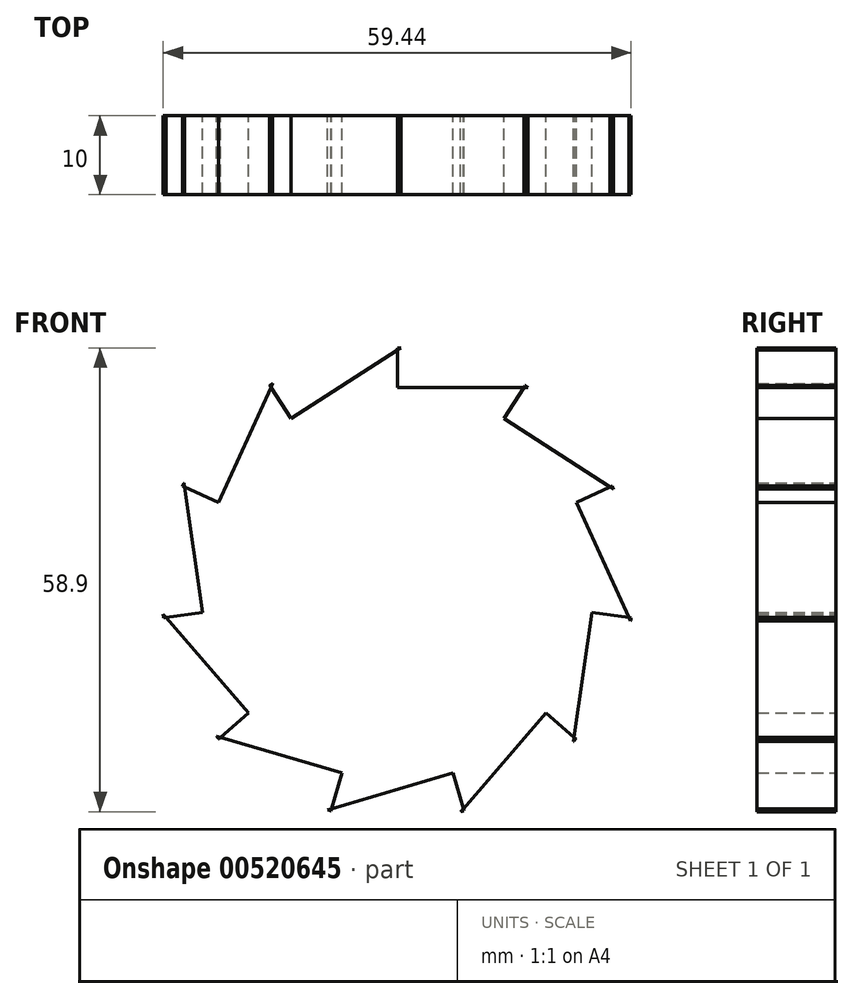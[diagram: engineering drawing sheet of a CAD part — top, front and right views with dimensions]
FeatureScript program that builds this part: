
annotation { "Feature Type Name" : "Feature", "Feature Type Description" : "" }
export const myFeature = defineFeature(function(context is Context, id is Id, definition is map)
    precondition{}
    {
        {
            var Q0;
            Q0=qCreatedBy(makeId("Front.planeOp"),FACE);
            var sketch = newSketch(context, id + "F0", { "sketchPlane" : qUnion([Q0])});
            skArc(sketch, "E0", {"start": v(16.58, 25) * mm, "mid": v(16.4, 25.12) * mm, "end": v(16.22, 25.24) * mm});
            skLineSegment(sketch, "E1", {"start": v(0, 25) * mm, "end": v(16.58, 25) * mm});
            skLineSegment(sketch, "E2", {"start": v(0, 30) * mm, "end": v(0, 25) * mm});
            skLineSegment(sketch, "E3.1.0", {"start": v(-13.52, 21.03) * mm, "end": v(0.43, 30) * mm});
            skLineSegment(sketch, "E3.1.1", {"start": v(-16.22, 25.24) * mm, "end": v(-13.52, 21.03) * mm});
            skLineSegment(sketch, "E3.2.0", {"start": v(-22.74, 10.39) * mm, "end": v(-15.85, 25.47) * mm});
            skLineSegment(sketch, "E3.2.1", {"start": v(-27.29, 12.46) * mm, "end": v(-22.74, 10.39) * mm});
            skLineSegment(sketch, "E3.3.0", {"start": v(-24.75, -3.56) * mm, "end": v(-27.1, 12.86) * mm});
            skLineSegment(sketch, "E3.3.1", {"start": v(-29.7, -4.27) * mm, "end": v(-24.75, -3.56) * mm});
            skLineSegment(sketch, "E3.4.0", {"start": v(-18.9, -16.37) * mm, "end": v(-29.75, -3.84) * mm});
            skLineSegment(sketch, "E3.4.1", {"start": v(-22.67, -19.65) * mm, "end": v(-18.9, -16.37) * mm});
            skLineSegment(sketch, "E3.5.0", {"start": v(-7.04, -23.99) * mm, "end": v(-22.95, -19.32) * mm});
            skLineSegment(sketch, "E3.5.1", {"start": v(-8.45, -28.78) * mm, "end": v(-7.04, -23.99) * mm});
            skLineSegment(sketch, "E3.6.0", {"start": v(7.04, -23.99) * mm, "end": v(-8.87, -28.66) * mm});
            skLineSegment(sketch, "E3.6.1", {"start": v(8.45, -28.78) * mm, "end": v(7.04, -23.99) * mm});
            skLineSegment(sketch, "E3.7.0", {"start": v(18.9, -16.37) * mm, "end": v(8.03, -28.9) * mm});
            skLineSegment(sketch, "E3.7.1", {"start": v(22.67, -19.65) * mm, "end": v(18.9, -16.37) * mm});
            skLineSegment(sketch, "E3.8.0", {"start": v(24.75, -3.56) * mm, "end": v(22.39, -19.97) * mm});
            skLineSegment(sketch, "E3.8.1", {"start": v(29.7, -4.27) * mm, "end": v(24.75, -3.56) * mm});
            skLineSegment(sketch, "E3.9.0", {"start": v(22.74, 10.39) * mm, "end": v(29.63, -4.7) * mm});
            skLineSegment(sketch, "E3.9.1", {"start": v(27.29, 12.46) * mm, "end": v(22.74, 10.39) * mm});
            skLineSegment(sketch, "E3.10.0", {"start": v(13.52, 21.03) * mm, "end": v(27.47, 12.07) * mm});
            skLineSegment(sketch, "E3.10.1", {"start": v(16.22, 25.24) * mm, "end": v(13.52, 21.03) * mm});
            skArc(sketch, "E4.trimOffspring", {"start": v(27.47, 12.07) * mm, "mid": v(27.38, 12.26) * mm, "end": v(27.29, 12.46) * mm});
            skArc(sketch, "E5.trimOffspring", {"start": v(29.63, -4.7) * mm, "mid": v(29.66, -4.48) * mm, "end": v(29.7, -4.27) * mm});
            skArc(sketch, "E6.trimOffspring", {"start": v(0.43, 30) * mm, "mid": v(0.22, 30) * mm, "end": v(0, 30) * mm});
            skArc(sketch, "E7.trimOffspring", {"start": v(-15.85, 25.47) * mm, "mid": v(-16.04, 25.35) * mm, "end": v(-16.22, 25.24) * mm});
            skArc(sketch, "E8.trimOffspring", {"start": v(-27.1, 12.86) * mm, "mid": v(-27.2, 12.66) * mm, "end": v(-27.29, 12.46) * mm});
            skArc(sketch, "E9.trimOffspring", {"start": v(-29.75, -3.84) * mm, "mid": v(-29.72, -4.05) * mm, "end": v(-29.7, -4.27) * mm});
            skArc(sketch, "E10.trimOffspring", {"start": v(-22.95, -19.32) * mm, "mid": v(-22.81, -19.48) * mm, "end": v(-22.67, -19.65) * mm});
            skArc(sketch, "E11.trimOffspring", {"start": v(-8.87, -28.66) * mm, "mid": v(-8.66, -28.72) * mm, "end": v(-8.45, -28.78) * mm});
            skArc(sketch, "E12.trimOffspring", {"start": v(8.03, -28.9) * mm, "mid": v(8.24, -28.85) * mm, "end": v(8.45, -28.78) * mm});
            skArc(sketch, "E13.trimOffspring", {"start": v(22.39, -19.97) * mm, "mid": v(22.53, -19.8) * mm, "end": v(22.67, -19.65) * mm});
            skSolve(sketch);
        }
        {
            var Q0;
            Q0 = qSketchRegion(id + "F0", true);
            extrude(context, id + "F1", {"entities" : qUnion([Q0]), "depth" : 10 * mm, "offsetDistance" : 25 * mm});
        }
    });
